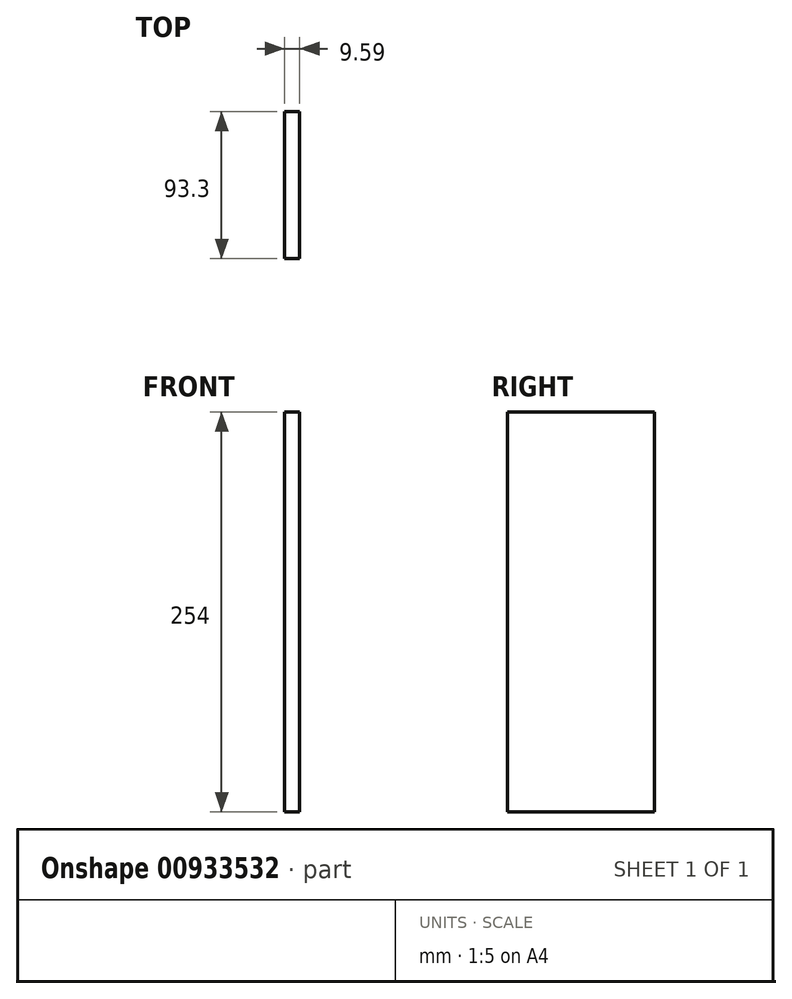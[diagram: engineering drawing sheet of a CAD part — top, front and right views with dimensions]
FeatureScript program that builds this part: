
annotation { "Feature Type Name" : "Feature", "Feature Type Description" : "" }
export const myFeature = defineFeature(function(context is Context, id is Id, definition is map)
    precondition{}
    {
        {
            var Q0;
            Q0=qCreatedBy(makeId("Top.planeOp"),FACE);
            var sketch = newSketch(context, id + "F0", { "sketchPlane" : qUnion([Q0])});
            skLineSegment(sketch, "E0.bottom", {"start": v(-60.62, -28.3) * mm, "end": v(-70.21, -28.3) * mm});
            skLineSegment(sketch, "E0.top", {"start": v(-60.62, 65) * mm, "end": v(-70.21, 65) * mm});
            skLineSegment(sketch, "E0.left", {"start": v(-60.62, -28.3) * mm, "end": v(-60.62, 65) * mm});
            skLineSegment(sketch, "E0.right", {"start": v(-70.21, -28.3) * mm, "end": v(-70.21, 65) * mm});
            skSolve(sketch);
        }
        {
            var Q0;
            Q0 = qSketchRegion(id + "F0", true);
            extrude(context, id + "F1", {"entities" : qUnion([Q0]), "depth" : 254 * mm, "offsetDistance" : 25.4 * mm});
        }
    });
